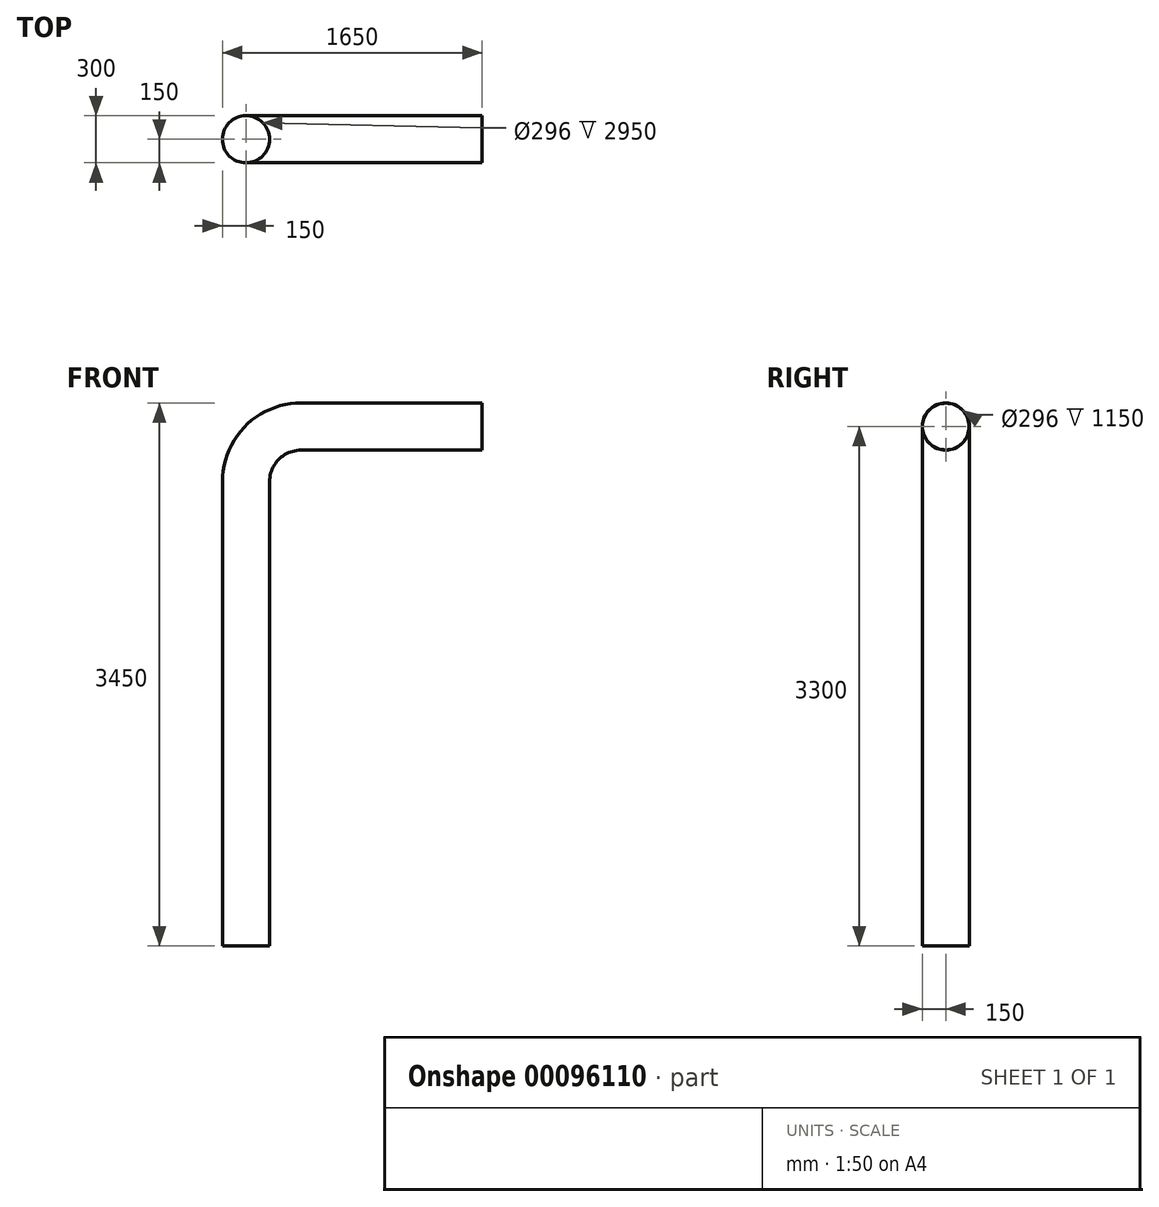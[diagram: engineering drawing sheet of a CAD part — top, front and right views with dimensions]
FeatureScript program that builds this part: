
annotation { "Feature Type Name" : "Feature", "Feature Type Description" : "" }
export const myFeature = defineFeature(function(context is Context, id is Id, definition is map)
    precondition{}
    {
        {
            var Q0;
            Q0=qCreatedBy(makeId("Front.planeOp"),FACE);
            var sketch = newSketch(context, id + "F0", { "sketchPlane" : qUnion([Q0])});
            skLineSegment(sketch, "E0", {"start": v(0, 0) * mm, "end": v(0, 2950) * mm});
            skLineSegment(sketch, "E1", {"start": v(350, 3300) * mm, "end": v(1500, 3300) * mm});
            skPoint(sketch, "E2.visualSharp", {"position": v(0, 3300) * mm});
            skArc(sketch, "E2.filletArc", {"start": v(350, 3300) * mm, "mid": v(102.51, 3197.49) * mm, "end": v(0, 2950) * mm});
            skSolve(sketch);
        }
        {
            var Q0;
            Q0=qCreatedBy(makeId("Top.planeOp"),FACE);
            var sketch = newSketch(context, id + "F1", { "sketchPlane" : qUnion([Q0])});
            skCircle(sketch, "E3", {"center": v(0, 0) * mm, "radius": 150 * mm});
            skCircle(sketch, "E4", {"center": v(0, 0) * mm, "radius": 148 * mm});
            skSolve(sketch);
        }
        {
            var Q0;
            Q0=makeQuery(id+"F1.imprint","IMPRINT",FACE,{"disambiguationData":[TD([[makeQuery(id+"F1.imprint","IMPRINT",EDGE,{"derivedFrom":sQuery(id+"F1.wireOp",EDGE,"E3")}),1.0]])]});
            var Q1;
            Q1=sQuery(id+"F0.wireOp",EDGE,"E0");
            var Q2;
            Q2=sQuery(id+"F0.wireOp",EDGE,"E2.filletArc");
            var Q3;
            Q3=sQuery(id+"F0.wireOp",EDGE,"E1");
            sweep(context, id + "F2", {"profiles" : qUnion([Q0]), "path" : qUnion([Q1, Q2, Q3])});
        }
    });
